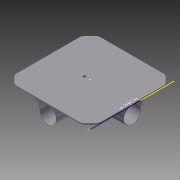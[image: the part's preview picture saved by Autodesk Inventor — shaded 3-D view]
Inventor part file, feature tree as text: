
AUTODESK INVENTOR PART (.ipt)
format: ipt  version: 2015 (Build 190159000, 159)  size: 204,288 bytes
history: native  units: in
note: dims shown in document units (in); Inventor stores cm internally (conversion verified against a paired STEP export)
features: sketch x9, extrude x7, pattern_circular x2, fillet x1
ambient origin geometry x8: Origin, YZ Plane, XZ Plane, XY Plane, X Axis, Y Axis, Z Axis, Center Point
bodies: Solid1 (feature_tree)
feature tree (19):
  extrude  "Extrusion1"  Depth=2.9528in
  sketch  "Sketch2"  dims[d2=5.9055in d3=5.9055in]
  extrude  "Extrusion2"  Depth=5.9055in
  pattern_circular  "Circular Pattern1"  Count=5  [1 undecoded]
  extrude  "Extrusion3"  Depth=0.5906in
  extrude  "Extrusion4"  Depth=0.5906in
  extrude  "Extrusion5"  Depth=1.9685in TaperAngle=0.0deg
  sketch  "Sketch7"  dims[d10=0.5906in]
  extrude  "Extrusion6"  Depth=0.5906in
  fillet  "Fillet1"  Radius=0.5906in
  pattern_circular  "Circular Pattern2"  [2 undecoded]
  extrude  "Extrusion7"  Depth=1.9685in TaperAngle=0.0deg
  sketch  "Sketch1"  dims[d0=2.9528in d1=2.9528in]
  sketch  "Sketch3"  dims[d4=0.0787in d5=0.0in]
  sketch  "Sketch4"  dims[d6=0.5906in]
  sketch  "Sketch5"  dims[d7=0.5906in]
  sketch  "Sketch6"  dims[d8=0.5906in]
  sketch  "Sketch8"  dims[d13=0.3937in d14=1.9685in d15=0.0in]
  sketch  "Sketch9"  dims[d16=1.5748in d17=360.0deg d19=0.5906in d20=0.5906in d21=1.9685in d22=0.0in d23=0.5906in d24=0.5906in d25=0.5906in d26=1.9685in d27=0.0in d28=0.5906in d29=0.5906in d30=1.9685in d31=0.0in d32=0.5906in d33=0.5906in d34=1.9685in d35=0.0in d36=0.3937in d37=1.5748in d38=360.0deg d40=0.1969in d41=0.1969in d42=0.0in]
note: 3 required parameter values undecoded (feature->parameter linkage not recoverable at this tier; creation-order binding heuristic only, values carry confidence <= 0.55)
